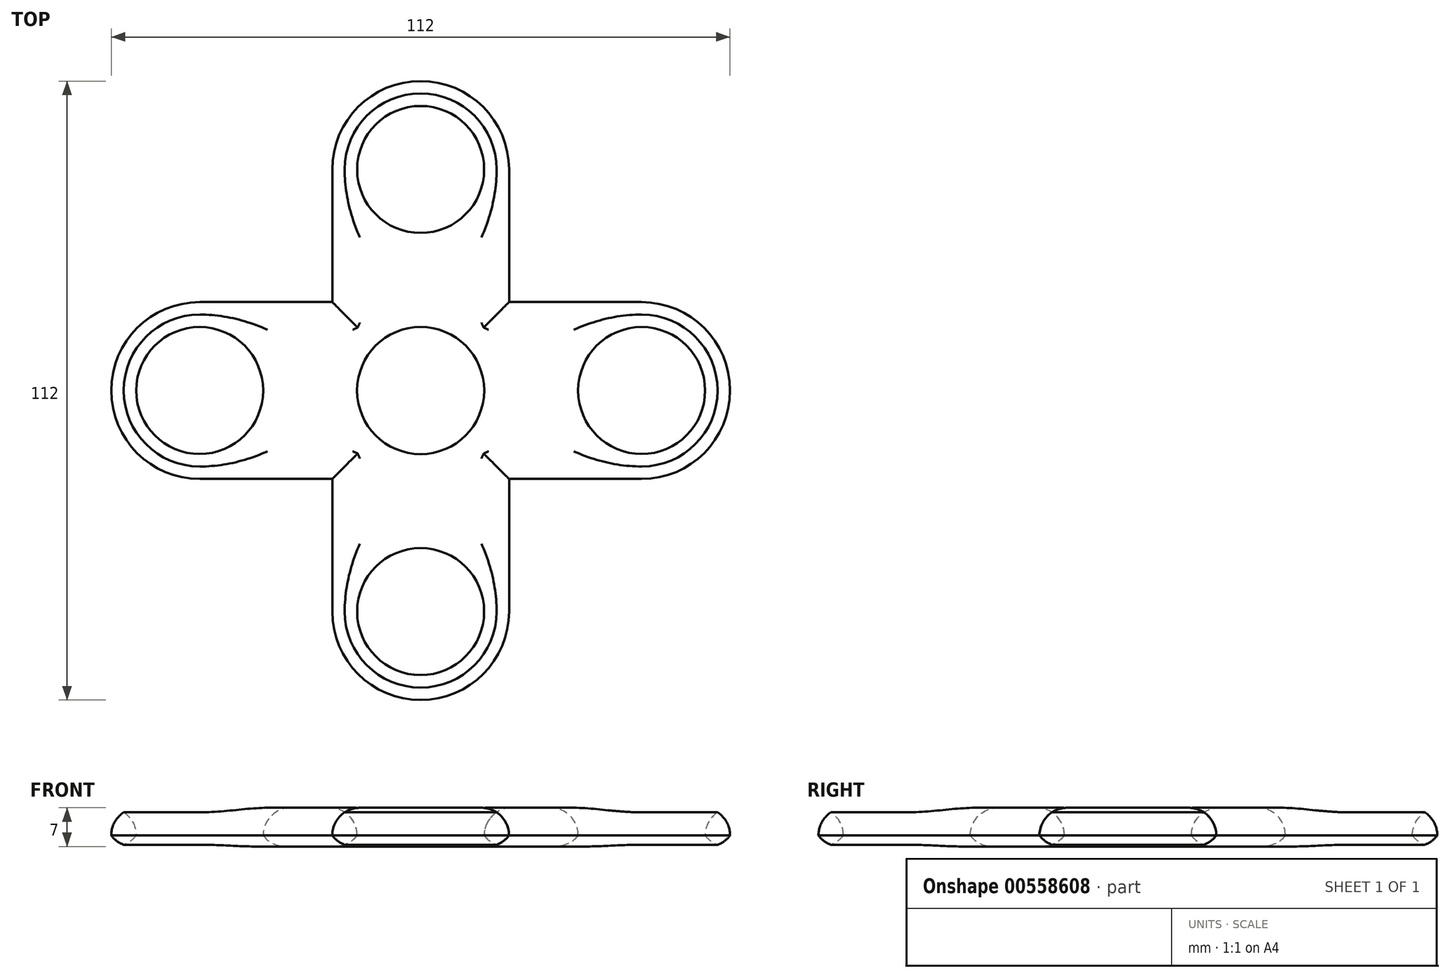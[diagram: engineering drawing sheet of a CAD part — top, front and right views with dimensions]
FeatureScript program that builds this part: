
annotation { "Feature Type Name" : "Feature", "Feature Type Description" : "" }
export const myFeature = defineFeature(function(context is Context, id is Id, definition is map)
    precondition{}
    {
        {
            var Q0;
            Q0=qCreatedBy(makeId("Top.planeOp"),FACE);
            var sketch = newSketch(context, id + "F0", { "sketchPlane" : qUnion([Q0])});
            skCircle(sketch, "E0", {"center": v(0, 0) * mm, "radius": 16 * mm});
            skCircle(sketch, "E1", {"center": v(0, -40) * mm, "radius": 16 * mm});
            skLineSegment(sketch, "E2", {"start": v(-16, 0) * mm, "end": v(-16, -40) * mm});
            skLineSegment(sketch, "E3", {"start": v(16, 0) * mm, "end": v(16, -40) * mm});
            skSolve(sketch);
        }
        {
            var Q0;
            {var subQ0=sQuery(id+"F0.wireOp",EDGE,"E0");var subQ1=makeQuery(id+"F0.imprint","INTERSECT",VERTEX,{"derivedFrom":[subQ0,sQuery(id+"F0.wireOp",EDGE,"E2")]});Q0=makeQuery(id+"F0.imprint","IMPRINT",FACE,{"disambiguationData":[TD([[makeQuery(id+"F0.imprint","IMPRINT",EDGE,{"disambiguationData":[TD([[subQ1,1.0]])],"derivedFrom":subQ0}),1.0]])]});}
            var Q1;
            {var subQ0=sQuery(id+"F0.wireOp",EDGE,"E2");Q1=makeQuery(id+"F0.imprint","IMPRINT",FACE,{"disambiguationData":[TD([[makeQuery(id+"F0.imprint","IMPRINT",EDGE,{"derivedFrom":subQ0}),1.0]])]});}
            var Q2;
            {var subQ0=sQuery(id+"F0.wireOp",EDGE,"E1");var subQ1=makeQuery(id+"F0.imprint","INTERSECT",VERTEX,{"derivedFrom":[subQ0,sQuery(id+"F0.wireOp",EDGE,"E2")]});Q2=makeQuery(id+"F0.imprint","IMPRINT",FACE,{"disambiguationData":[TD([[makeQuery(id+"F0.imprint","IMPRINT",EDGE,{"disambiguationData":[TD([[subQ1,1.0]])],"derivedFrom":subQ0}),1.0]])]});}
            extrude(context, id + "F1", {"entities" : qUnion([Q0, Q1, Q2]), "depth" : 7 * mm, "offsetDistance" : 25 * mm});
        }
        {
            var Q0;
            Q0=makeQuery(id+"F1.opExtrude","CAP_FACE",FACE,{"disambiguationData":[OSD([sQuery(id+"F0.wireOp",EDGE,"E0"),sQuery(id+"F0.wireOp",EDGE,"E1"),sQuery(id+"F0.wireOp",EDGE,"E2"),sQuery(id+"F0.wireOp",EDGE,"E3")])],"isStart":false});
            var sketch = newSketch(context, id + "F2", { "sketchPlane" : qUnion([Q0])});
            skCircle(sketch, "E4", {"center": v(0, 0) * mm, "radius": 11.5 * mm});
            skCircle(sketch, "E5", {"center": v(0, -40) * mm, "radius": 11.49 * mm});
            skSolve(sketch);
        }
        {
            var Q0;
            Q0=makeQuery(id+"F2.imprint","IMPRINT",FACE,{"disambiguationData":[TD([[makeQuery(id+"F2.imprint","IMPRINT",EDGE,{"derivedFrom":sQuery(id+"F2.wireOp",EDGE,"E4")}),1.0]])]});
            var Q1;
            Q1=makeQuery(id+"F2.imprint","IMPRINT",FACE,{"disambiguationData":[TD([[makeQuery(id+"F2.imprint","IMPRINT",EDGE,{"derivedFrom":sQuery(id+"F2.wireOp",EDGE,"E5")}),1.0]])]});
            extrude(context, id + "F3", {"entities" : qUnion([Q0, Q1]), "operationType" : NewBodyOperationType.REMOVE, "oppositeDirection" : true, "depth" : 7 * mm, "offsetDistance" : 25 * mm});
        }
        {
            var Q0;
            Q0=qCreatedBy(makeId("Front.planeOp"),FACE);
            var sketch = newSketch(context, id + "F4", { "sketchPlane" : qUnion([Q0])});
            skLineSegment(sketch, "E6", {"start": v(0, 0) * mm, "end": v(0, 26.08) * mm});
            skSolve(sketch);
        }
        {
            var Q0;
            Q0=makeQuery(id+"F1.opExtrude","SWEPT_BODY",BODY,{"disambiguationData":[OSD([sQuery(id+"F0.wireOp",EDGE,"E0"),sQuery(id+"F0.wireOp",EDGE,"E1"),sQuery(id+"F0.wireOp",EDGE,"E2"),sQuery(id+"F0.wireOp",EDGE,"E3")])]});
            var Q1;
            Q1=sQuery(id+"F4.wireOp",EDGE,"E6");
            circularPattern(context, id + "F5", {"operationType" : NewBodyOperationType.ADD, "entities" : qUnion([Q0]), "axis" : qUnion([Q1]), "angle" : 360 * degree, "instanceCount" : 4, "equalSpace" : true});
        }
        {
            var Q0;
            {var subQ0=makeQuery(id+"F1.opExtrude","CAP_FACE",FACE,{"disambiguationData":[OSD([sQuery(id+"F0.wireOp",EDGE,"E0"),sQuery(id+"F0.wireOp",EDGE,"E1"),sQuery(id+"F0.wireOp",EDGE,"E2"),sQuery(id+"F0.wireOp",EDGE,"E3")])],"isStart":false});Q0=makeQuery(id+"F5.boolean.opBoolean","MERGE",FACE,{"derivedFrom":[subQ0,makeQuery(id+"F5.opPattern","COPY",FACE,{"derivedFrom":subQ0,"instanceName":"1"}),makeQuery(id+"F5.opPattern","COPY",FACE,{"derivedFrom":subQ0,"instanceName":"2"}),makeQuery(id+"F5.opPattern","COPY",FACE,{"derivedFrom":subQ0,"instanceName":"3"})]});}
            fillet(context, id + "F6", {"entities" : qUnion([Q0]), "radius" : 5 * mm, "tangentPropagation" : true, "allowEdgeOverflow" : false});
        }
        {
            var Q0;
            {var subQ0=makeQuery(id+"F1.opExtrude","CAP_FACE",FACE,{"disambiguationData":[OSD([sQuery(id+"F0.wireOp",EDGE,"E0"),sQuery(id+"F0.wireOp",EDGE,"E1"),sQuery(id+"F0.wireOp",EDGE,"E2"),sQuery(id+"F0.wireOp",EDGE,"E3")])],"isStart":true});Q0=makeQuery(id+"F5.boolean.opBoolean","MERGE",FACE,{"derivedFrom":[subQ0,makeQuery(id+"F5.opPattern","COPY",FACE,{"derivedFrom":subQ0,"instanceName":"1"}),makeQuery(id+"F5.opPattern","COPY",FACE,{"derivedFrom":subQ0,"instanceName":"2"}),makeQuery(id+"F5.opPattern","COPY",FACE,{"derivedFrom":subQ0,"instanceName":"3"})]});}
            fillet(context, id + "F7", {"entities" : qUnion([Q0]), "radius" : 5 * mm, "tangentPropagation" : true, "allowEdgeOverflow" : false});
        }
    });
